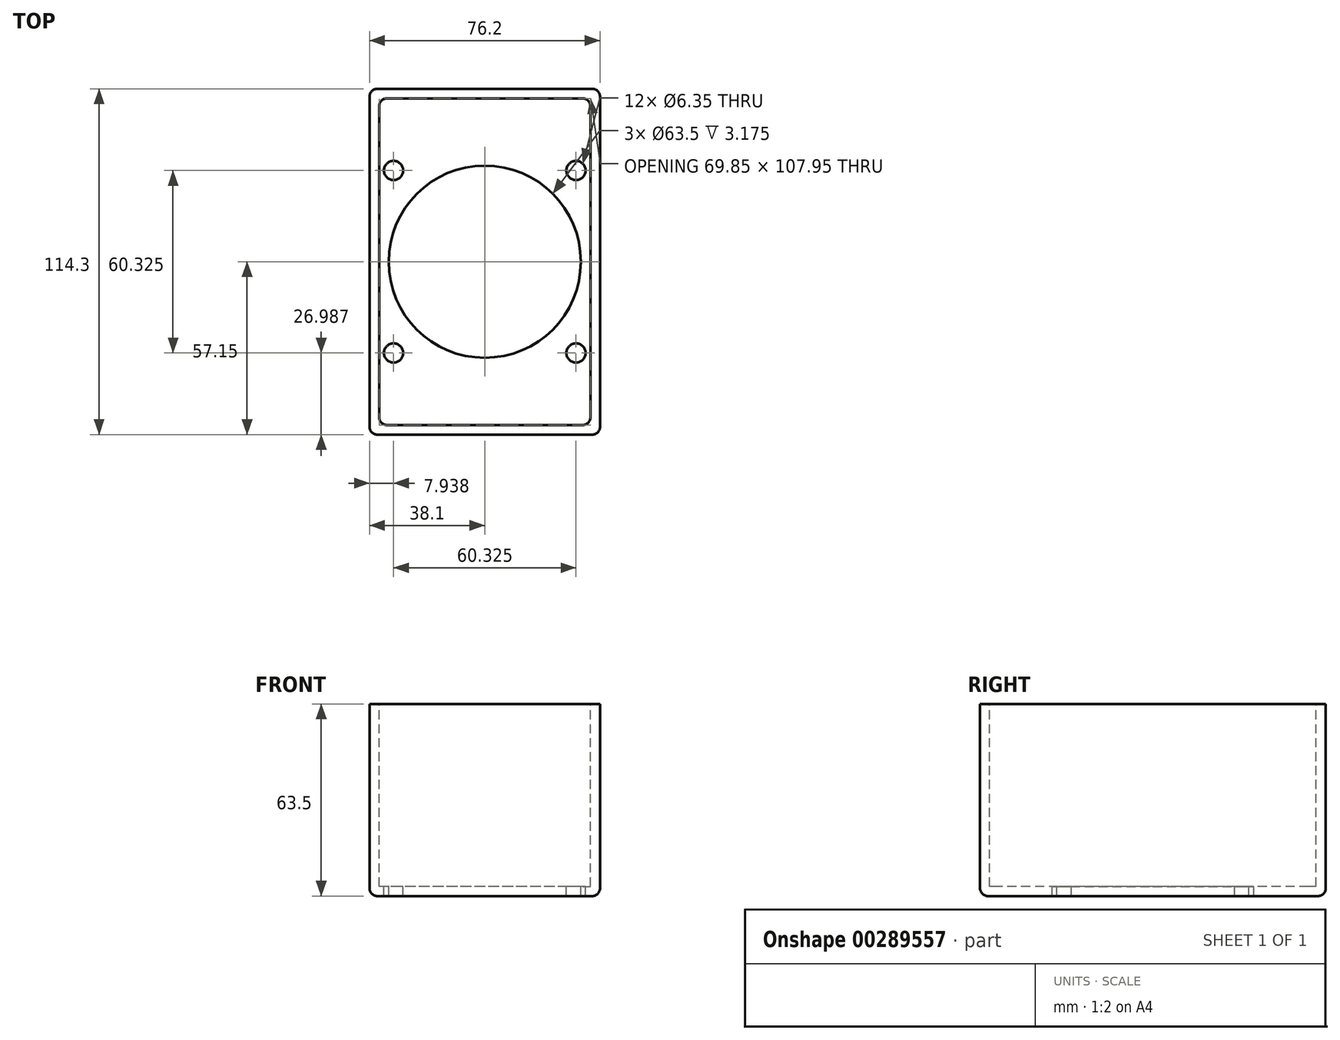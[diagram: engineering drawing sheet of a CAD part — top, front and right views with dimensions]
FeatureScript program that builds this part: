
annotation { "Feature Type Name" : "Feature", "Feature Type Description" : "" }
export const myFeature = defineFeature(function(context is Context, id is Id, definition is map)
    precondition{}
    {
        {
            var Q0;
            Q0=qCreatedBy(makeId("Top.planeOp"),FACE);
            var sketch = newSketch(context, id + "F0", { "sketchPlane" : qUnion([Q0])});
            skLineSegment(sketch, "E0.bottom", {"start": v(38.1, 57.15) * mm, "end": v(-38.1, 57.15) * mm});
            skLineSegment(sketch, "E0.top", {"start": v(38.1, -57.15) * mm, "end": v(-38.1, -57.15) * mm});
            skLineSegment(sketch, "E0.left", {"start": v(38.1, 57.15) * mm, "end": v(38.1, -57.15) * mm});
            skLineSegment(sketch, "E0.right", {"start": v(-38.1, 57.15) * mm, "end": v(-38.1, -57.15) * mm});
            skPoint(sketch, "E0.middle", {"position": v(0, 0) * mm});
            skSolve(sketch);
        }
        {
            var Q0;
            Q0 = qSketchRegion(id + "F0", true);
            extrude(context, id + "F1", {"entities" : qUnion([Q0]), "depth" : 63.5 * mm});
        }
        {
            var Q0;
            Q0=makeQuery(id+"F1.opExtrude","CAP_FACE",FACE,{"disambiguationData":[OSD([sQuery(id+"F0.wireOp",EDGE,"E0.bottom"),sQuery(id+"F0.wireOp",EDGE,"E0.top"),sQuery(id+"F0.wireOp",EDGE,"E0.left"),sQuery(id+"F0.wireOp",EDGE,"E0.right")])],"isStart":false});
            var sketch = newSketch(context, id + "F2", { "sketchPlane" : qUnion([Q0])});
            skLineSegment(sketch, "E1.bottom", {"start": v(34.93, 53.98) * mm, "end": v(-34.93, 53.98) * mm});
            skLineSegment(sketch, "E1.top", {"start": v(34.93, -53.98) * mm, "end": v(-34.93, -53.98) * mm});
            skLineSegment(sketch, "E1.left", {"start": v(34.93, 53.98) * mm, "end": v(34.93, -53.98) * mm});
            skLineSegment(sketch, "E1.right", {"start": v(-34.93, 53.98) * mm, "end": v(-34.93, -53.98) * mm});
            skPoint(sketch, "E1.middle", {"position": v(0, 0) * mm});
            skSolve(sketch);
        }
        {
            var Q0;
            Q0 = qSketchRegion(id + "F2", true);
            extrude(context, id + "F3", {"entities" : qUnion([Q0]), "operationType" : NewBodyOperationType.REMOVE, "oppositeDirection" : true, "depth" : 60.32 * mm});
        }
        {
            var Q0;
            Q0=makeQuery(id+"F3.boolean.opBoolean","COPY",EDGE,{"derivedFrom":makeQuery(id+"F3.opExtrude","SWEPT_EDGE",EDGE,{"disambiguationData":[OSD([sQuery(id+"F2.wireOp",EDGE,"E1.bottom"),sQuery(id+"F2.wireOp",EDGE,"E1.left")])]})});
            var Q1;
            Q1=makeQuery(id+"F3.boolean.opBoolean","COPY",EDGE,{"derivedFrom":makeQuery(id+"F3.opExtrude","SWEPT_EDGE",EDGE,{"disambiguationData":[OSD([sQuery(id+"F2.wireOp",EDGE,"E1.top"),sQuery(id+"F2.wireOp",EDGE,"E1.left")])]})});
            var Q2;
            Q2=makeQuery(id+"F3.boolean.opBoolean","COPY",EDGE,{"derivedFrom":makeQuery(id+"F3.opExtrude","SWEPT_EDGE",EDGE,{"disambiguationData":[OSD([sQuery(id+"F2.wireOp",EDGE,"E1.top"),sQuery(id+"F2.wireOp",EDGE,"E1.right")])]})});
            var Q3;
            Q3=makeQuery(id+"F3.boolean.opBoolean","COPY",EDGE,{"derivedFrom":makeQuery(id+"F3.opExtrude","SWEPT_EDGE",EDGE,{"disambiguationData":[OSD([sQuery(id+"F2.wireOp",EDGE,"E1.bottom"),sQuery(id+"F2.wireOp",EDGE,"E1.right")])]})});
            var Q4;
            Q4=makeQuery(id+"F1.opExtrude","SWEPT_EDGE",EDGE,{"disambiguationData":[OSD([sQuery(id+"F0.wireOp",EDGE,"E0.top"),sQuery(id+"F0.wireOp",EDGE,"E0.left")])]});
            var Q5;
            Q5=makeQuery(id+"F1.opExtrude","SWEPT_EDGE",EDGE,{"disambiguationData":[OSD([sQuery(id+"F0.wireOp",EDGE,"E0.bottom"),sQuery(id+"F0.wireOp",EDGE,"E0.left")])]});
            var Q6;
            Q6=makeQuery(id+"F1.opExtrude","SWEPT_EDGE",EDGE,{"disambiguationData":[OSD([sQuery(id+"F0.wireOp",EDGE,"E0.top"),sQuery(id+"F0.wireOp",EDGE,"E0.right")])]});
            var Q7;
            Q7=makeQuery(id+"F1.opExtrude","SWEPT_EDGE",EDGE,{"disambiguationData":[OSD([sQuery(id+"F0.wireOp",EDGE,"E0.bottom"),sQuery(id+"F0.wireOp",EDGE,"E0.right")])]});
            var Q8;
            Q8=makeQuery(id+"F1.opExtrude","CAP_EDGE",EDGE,{"disambiguationData":[OSD([sQuery(id+"F0.wireOp",EDGE,"E0.right")])],"isStart":true});
            var Q9;
            Q9=makeQuery(id+"F1.opExtrude","CAP_EDGE",EDGE,{"disambiguationData":[OSD([sQuery(id+"F0.wireOp",EDGE,"E0.bottom")])],"isStart":true});
            var Q10;
            Q10=makeQuery(id+"F1.opExtrude","CAP_EDGE",EDGE,{"disambiguationData":[OSD([sQuery(id+"F0.wireOp",EDGE,"E0.top")])],"isStart":true});
            var Q11;
            Q11=makeQuery(id+"F1.opExtrude","CAP_EDGE",EDGE,{"disambiguationData":[OSD([sQuery(id+"F0.wireOp",EDGE,"E0.left")])],"isStart":true});
            fillet(context, id + "F4", {"entities" : qUnion([Q0, Q1, Q2, Q3, Q4, Q5, Q6, Q7, Q8, Q9, Q10, Q11]), "radius" : 2.54 * mm, "tangentPropagation" : true, "allowEdgeOverflow" : false});
        }
        {
            var Q0;
            Q0=makeQuery(id+"F3.boolean.opBoolean","COPY",FACE,{"derivedFrom":makeQuery(id+"F3.opExtrude","CAP_FACE",FACE,{"disambiguationData":[OSD([sQuery(id+"F2.wireOp",EDGE,"E1.bottom"),sQuery(id+"F2.wireOp",EDGE,"E1.top"),sQuery(id+"F2.wireOp",EDGE,"E1.left"),sQuery(id+"F2.wireOp",EDGE,"E1.right")])],"isStart":false})});
            var sketch = newSketch(context, id + "F5", { "sketchPlane" : qUnion([Q0])});
            skCircle(sketch, "E2", {"center": v(0, 0) * mm, "radius": 31.75 * mm});
            skSolve(sketch);
        }
        {
            var Q0;
            Q0 = qSketchRegion(id + "F5", true);
            extrude(context, id + "F6", {"entities" : qUnion([Q0]), "operationType" : NewBodyOperationType.REMOVE, "endBound" : BoundingType.UP_TO_NEXT, "oppositeDirection" : true, "depth" : 25.4 * mm});
        }
        {
            var Q0;
            Q0=makeQuery(id+"F3.boolean.opBoolean","COPY",FACE,{"derivedFrom":makeQuery(id+"F3.opExtrude","CAP_FACE",FACE,{"disambiguationData":[OSD([sQuery(id+"F2.wireOp",EDGE,"E1.bottom"),sQuery(id+"F2.wireOp",EDGE,"E1.top"),sQuery(id+"F2.wireOp",EDGE,"E1.left"),sQuery(id+"F2.wireOp",EDGE,"E1.right")])],"isStart":false})});
            var sketch = newSketch(context, id + "F7", { "sketchPlane" : qUnion([Q0])});
            skLineSegment(sketch, "E3.bottom", {"start": v(30.16, 30.16) * mm, "end": v(-30.16, 30.16) * mm, "construction": true});
            skLineSegment(sketch, "E3.top", {"start": v(30.16, -30.16) * mm, "end": v(-30.16, -30.16) * mm, "construction": true});
            skLineSegment(sketch, "E3.left", {"start": v(30.16, 30.16) * mm, "end": v(30.16, -30.16) * mm, "construction": true});
            skLineSegment(sketch, "E3.right", {"start": v(-30.16, 30.16) * mm, "end": v(-30.16, -30.16) * mm, "construction": true});
            skPoint(sketch, "E3.middle", {"position": v(0, 0) * mm});
            skCircle(sketch, "E4", {"center": v(30.16, 30.16) * mm, "radius": 3.18 * mm});
            skCircle(sketch, "E5", {"center": v(30.16, -30.16) * mm, "radius": 3.18 * mm});
            skCircle(sketch, "E6", {"center": v(-30.16, -30.16) * mm, "radius": 3.18 * mm});
            skCircle(sketch, "E7", {"center": v(-30.16, 30.16) * mm, "radius": 3.18 * mm});
            skSolve(sketch);
        }
        {
            var Q0;
            Q0 = qSketchRegion(id + "F7", true);
            extrude(context, id + "F8", {"entities" : qUnion([Q0]), "operationType" : NewBodyOperationType.REMOVE, "endBound" : BoundingType.UP_TO_NEXT, "oppositeDirection" : true, "depth" : 25.4 * mm});
        }
    });
